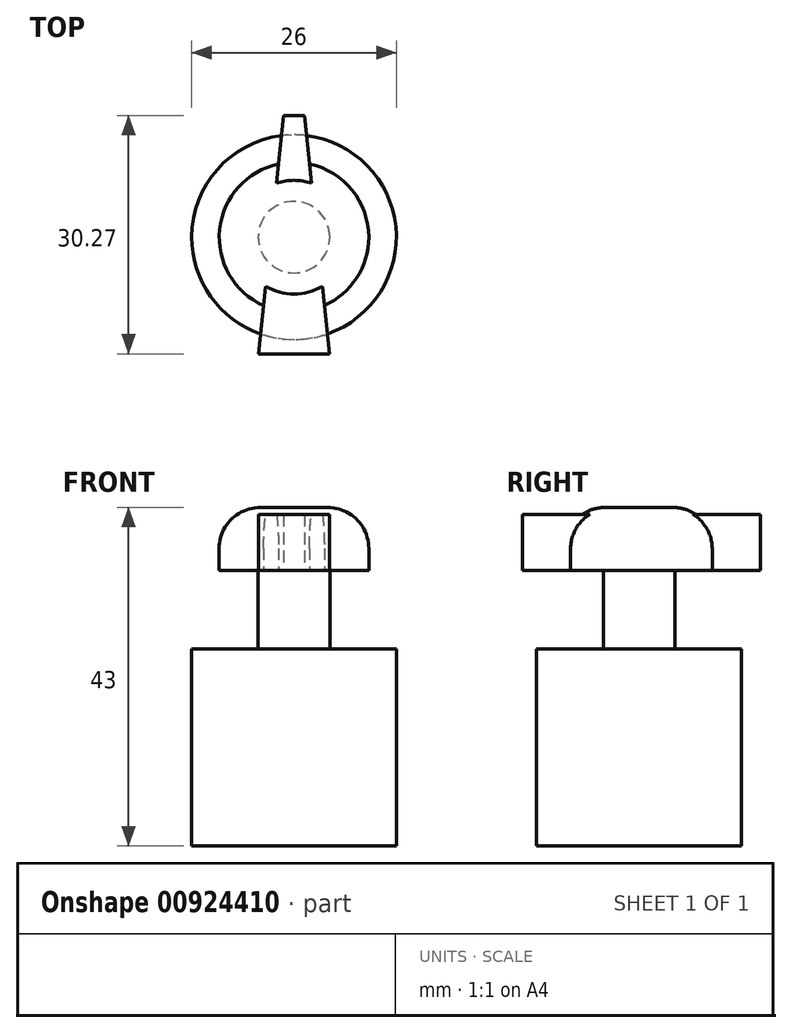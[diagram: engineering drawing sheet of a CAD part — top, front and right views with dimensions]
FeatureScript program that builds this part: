
annotation { "Feature Type Name" : "Feature", "Feature Type Description" : "" }
export const myFeature = defineFeature(function(context is Context, id is Id, definition is map)
    precondition{}
    {
        {
            var Q0;
            Q0=qCreatedBy(makeId("Top.planeOp"),FACE);
            var sketch = newSketch(context, id + "F0", { "sketchPlane" : qUnion([Q0])});
            skCircle(sketch, "E0", {"center": v(0, 0) * mm, "radius": 9.5 * mm});
            skCircle(sketch, "E1", {"center": v(0, 0) * mm, "radius": 16 * mm, "construction": true});
            skSolve(sketch);
        }
        {
            var Q0;
            Q0 = qSketchRegion(id + "F0", true);
            var Q1;
            Q1 = qConstructionFilter(qBodyType(qCreatedBy(id + "F0" ,EDGE), BodyType.WIRE), ConstructionObject.NO);
            extrude(context, id + "F1", {"entities" : qUnion([Q0]), "surfaceEntities" : qUnion([Q1]), "depth" : 8 * mm, "offsetDistance" : 25 * mm});
        }
        {
            var Q0;
            Q0=makeQuery(id+"F1.opExtrude","CAP_EDGE",EDGE,{"disambiguationData":[OSD([sQuery(id+"F0.wireOp",EDGE,"E0")])],"isStart":false});
            fillet(context, id + "F2", {"entities" : qUnion([Q0]), "radius" : 5.2 * mm, "tangentPropagation" : true, "allowEdgeOverflow" : false});
        }
        {
            var Q0;
            Q0=qCreatedBy(makeId("Top.planeOp"),FACE);
            var sketch = newSketch(context, id + "F3", { "sketchPlane" : qUnion([Q0])});
            skCircle(sketch, "E2", {"center": v(0, 0) * mm, "radius": 15.5 * mm, "construction": true});
            skLineSegment(sketch, "E3", {"start": v(1.32, 15.44) * mm, "end": v(-1.32, 15.44) * mm});
            skLineSegment(sketch, "E4", {"start": v(-1.32, 15.44) * mm, "end": v(-4.5, -14.83) * mm});
            skLineSegment(sketch, "E5", {"start": v(-4.5, -14.83) * mm, "end": v(4.5, -14.83) * mm});
            skLineSegment(sketch, "E6", {"start": v(4.5, -14.83) * mm, "end": v(1.32, 15.44) * mm});
            skLineSegment(sketch, "E7", {"start": v(0, 15.44) * mm, "end": v(0, -15.5) * mm, "construction": true});
            skPoint(sketch, "E8", {"position": v(0, -14.83) * mm});
            skLineSegment(sketch, "E9.MirrorCS", {"start": v(-4.5, -14.83) * mm, "end": v(-1.32, 15.44) * mm});
            skLineSegment(sketch, "E10.MirrorCS", {"start": v(1.32, 15.44) * mm, "end": v(4.5, -14.83) * mm});
            skSolve(sketch);
        }
        {
            var Q0;
            Q0 = qSketchRegion(id + "F3", true);
            extrude(context, id + "F4", {"entities" : qUnion([Q0]), "operationType" : NewBodyOperationType.ADD, "depth" : 7.1 * mm, "offsetDistance" : 25 * mm});
        }
        {
            var Q0;
            Q0=makeQuery(id+"F4.boolean.opBoolean","MERGE",FACE,{"derivedFrom":[makeQuery(id+"F1.opExtrude","CAP_FACE",FACE,{"disambiguationData":[OSD([sQuery(id+"F0.wireOp",EDGE,"E0")])],"isStart":true}),makeQuery(id+"F4.opExtrude","CAP_FACE",FACE,{"disambiguationData":[OSD([sQuery(id+"F3.wireOp",EDGE,"E3"),sQuery(id+"F3.wireOp",EDGE,"E5"),sQuery(id+"F3.wireOp",EDGE,"E9.MirrorCS"),sQuery(id+"F3.wireOp",EDGE,"E10.MirrorCS")])],"isStart":true})]});
            var sketch = newSketch(context, id + "F5", { "sketchPlane" : qUnion([Q0])});
            skCircle(sketch, "E11", {"center": v(0, 0) * mm, "radius": 4.55 * mm});
            skSolve(sketch);
        }
        {
            var Q0;
            Q0=makeQuery(id+"F5.imprint","IMPRINT",FACE,{"disambiguationData":[TD([[makeQuery(id+"F5.imprint","IMPRINT",EDGE,{"derivedFrom":sQuery(id+"F5.wireOp",EDGE,"E11")}),1.0]])]});
            extrude(context, id + "F6", {"entities" : qUnion([Q0]), "operationType" : NewBodyOperationType.ADD, "depth" : 35 * mm, "offsetDistance" : 25 * mm});
        }
        {
            var Q0;
            Q0=makeQuery(id+"F6.opExtrude","CAP_FACE",FACE,{"disambiguationData":[OSD([sQuery(id+"F5.wireOp",EDGE,"E11")])],"isStart":false});
            var sketch = newSketch(context, id + "F7", { "sketchPlane" : qUnion([Q0])});
            skCircle(sketch, "E12", {"center": v(0, 0) * mm, "radius": 13 * mm});
            skSolve(sketch);
        }
        {
            var Q0;
            Q0=makeQuery(id+"F7.imprint","IMPRINT",FACE,{"disambiguationData":[TD([[makeQuery(id+"F7.imprint","IMPRINT",EDGE,{"derivedFrom":sQuery(id+"F7.wireOp",EDGE,"E12")}),1.0]])]});
            extrude(context, id + "F8", {"entities" : qUnion([Q0]), "operationType" : NewBodyOperationType.ADD, "oppositeDirection" : true, "depth" : 25 * mm, "offsetDistance" : 25 * mm});
        }
    });
